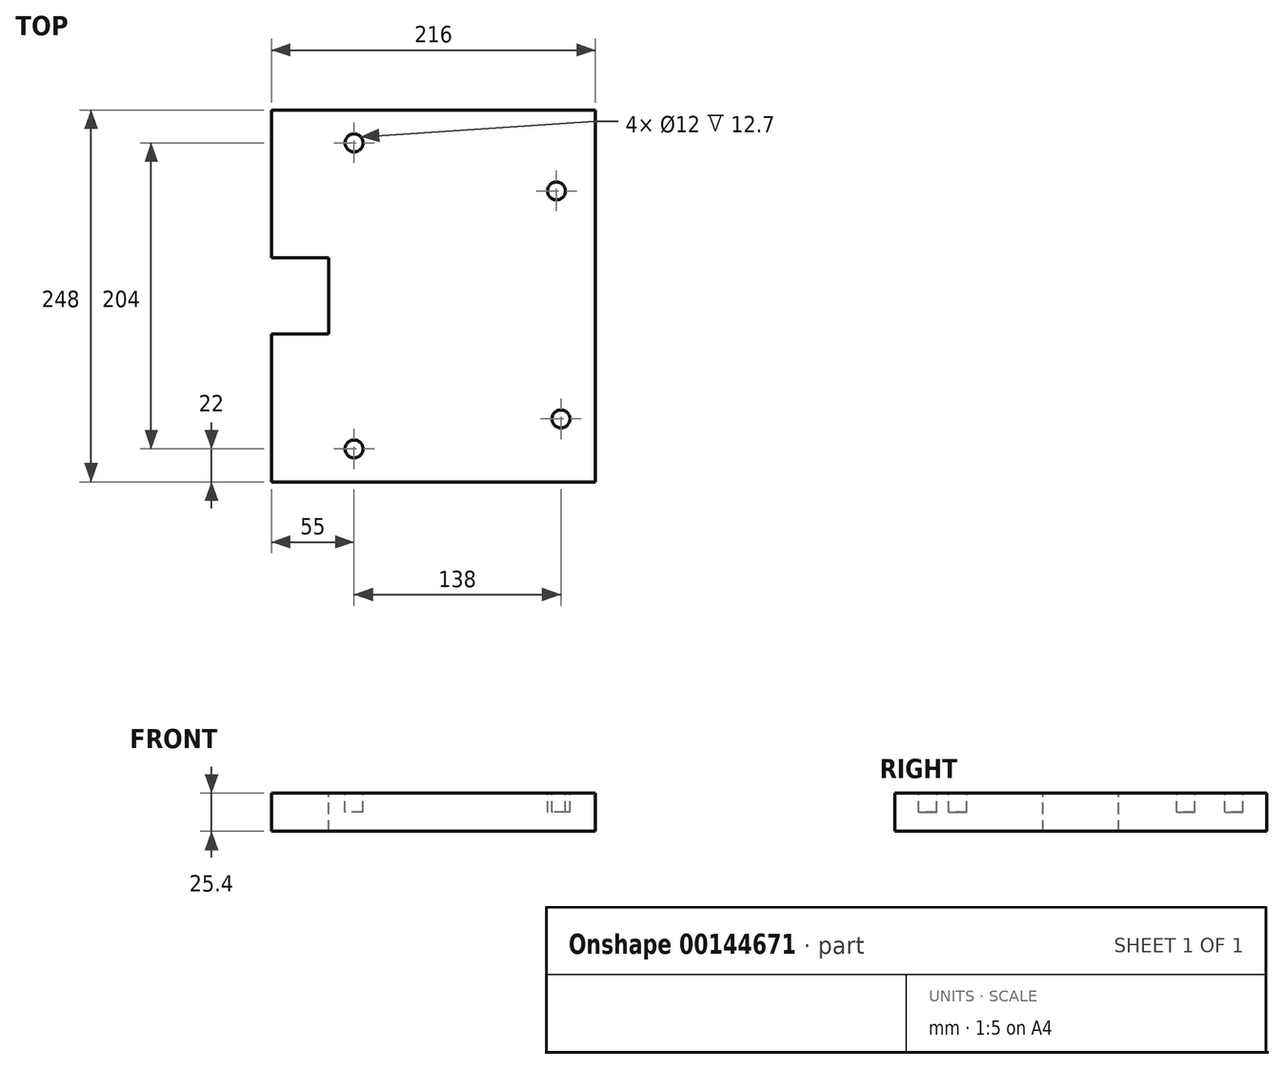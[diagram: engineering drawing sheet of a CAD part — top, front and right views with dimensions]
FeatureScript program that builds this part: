
annotation { "Feature Type Name" : "Feature", "Feature Type Description" : "" }
export const myFeature = defineFeature(function(context is Context, id is Id, definition is map)
    precondition{}
    {
        {
            var Q0;
            Q0=qCreatedBy(makeId("Front.planeOp"),FACE);
            var sketch = newSketch(context, id + "F0", { "sketchPlane" : qUnion([Q0])});
            skLineSegment(sketch, "E0.bottom", {"start": v(0, 0) * mm, "end": v(-216, 0) * mm});
            skLineSegment(sketch, "E0.top", {"start": v(0, 25.4) * mm, "end": v(-216, 25.4) * mm});
            skLineSegment(sketch, "E0.left", {"start": v(0, 0) * mm, "end": v(0, 25.4) * mm});
            skLineSegment(sketch, "E0.right", {"start": v(-216, 0) * mm, "end": v(-216, 25.4) * mm});
            skSolve(sketch);
        }
        {
            var Q0;
            Q0=makeQuery(id+"F0.imprint","IMPRINT",FACE,{"disambiguationData":[TD([[makeQuery(id+"F0.imprint","IMPRINT",EDGE,{"derivedFrom":sQuery(id+"F0.wireOp",EDGE,"E0.bottom")}),-1.0]])]});
            extrude(context, id + "F1", {"entities" : qUnion([Q0]), "oppositeDirection" : true, "depth" : 248 * mm});
        }
        {
            var Q0;
            Q0=makeQuery(id+"F1.opExtrude","SWEPT_FACE",FACE,{"disambiguationData":[OSD([sQuery(id+"F0.wireOp",EDGE,"E0.top")])]});
            var sketch = newSketch(context, id + "F2", { "sketchPlane" : qUnion([Q0])});
            skCircle(sketch, "E1", {"center": v(-26, 194) * mm, "radius": 6 * mm});
            skCircle(sketch, "E2", {"center": v(-23, 42) * mm, "radius": 6 * mm});
            skCircle(sketch, "E3", {"center": v(-161, 226) * mm, "radius": 6 * mm});
            skCircle(sketch, "E4", {"center": v(-161, 22) * mm, "radius": 6 * mm});
            skSolve(sketch);
        }
        {
            var Q0;
            Q0=makeQuery(id+"F2.imprint","IMPRINT",FACE,{"disambiguationData":[TD([[makeQuery(id+"F2.imprint","IMPRINT",EDGE,{"derivedFrom":sQuery(id+"F2.wireOp",EDGE,"E3")}),1.0]])]});
            var Q1;
            Q1=makeQuery(id+"F2.imprint","IMPRINT",FACE,{"disambiguationData":[TD([[makeQuery(id+"F2.imprint","IMPRINT",EDGE,{"derivedFrom":sQuery(id+"F2.wireOp",EDGE,"E4")}),1.0]])]});
            var Q2;
            Q2=makeQuery(id+"F2.imprint","IMPRINT",FACE,{"disambiguationData":[TD([[makeQuery(id+"F2.imprint","IMPRINT",EDGE,{"derivedFrom":sQuery(id+"F2.wireOp",EDGE,"E1")}),1.0]])]});
            var Q3;
            Q3=makeQuery(id+"F2.imprint","IMPRINT",FACE,{"disambiguationData":[TD([[makeQuery(id+"F2.imprint","IMPRINT",EDGE,{"derivedFrom":sQuery(id+"F2.wireOp",EDGE,"E2")}),1.0]])]});
            extrude(context, id + "F3", {"entities" : qUnion([Q0, Q1, Q2, Q3]), "operationType" : NewBodyOperationType.REMOVE, "oppositeDirection" : true, "depth" : 12.7 * mm});
        }
        {
            var Q0;
            Q0=makeQuery(id+"F1.opExtrude","SWEPT_FACE",FACE,{"disambiguationData":[OSD([sQuery(id+"F0.wireOp",EDGE,"E0.top")])]});
            var sketch = newSketch(context, id + "F4", { "sketchPlane" : qUnion([Q0])});
            skLineSegment(sketch, "E5", {"start": v(-216, 248) * mm, "end": v(-216, 149.4) * mm, "construction": true});
            skLineSegment(sketch, "E6", {"start": v(-216, 0) * mm, "end": v(-216, 98.6) * mm, "construction": true});
            skLineSegment(sketch, "E7.bottom", {"start": v(-216, 149.4) * mm, "end": v(-178, 149.4) * mm});
            skLineSegment(sketch, "E7.top", {"start": v(-216, 98.6) * mm, "end": v(-178, 98.6) * mm});
            skLineSegment(sketch, "E7.left", {"start": v(-216, 149.4) * mm, "end": v(-216, 98.6) * mm});
            skLineSegment(sketch, "E7.right", {"start": v(-178, 149.4) * mm, "end": v(-178, 98.6) * mm});
            skSolve(sketch);
        }
        {
            var Q0;
            Q0=makeQuery(id+"F4.imprint","IMPRINT",FACE,{"disambiguationData":[TD([[makeQuery(id+"F4.imprint","IMPRINT",EDGE,{"derivedFrom":sQuery(id+"F4.wireOp",EDGE,"E7.bottom")}),-1.0]])]});
            var Q1;
            Q1=makeQuery(id+"F1.opExtrude","SWEPT_FACE",FACE,{"disambiguationData":[OSD([sQuery(id+"F0.wireOp",EDGE,"E0.bottom")])]});
            extrude(context, id + "F5", {"entities" : qUnion([Q0]), "operationType" : NewBodyOperationType.REMOVE, "endBound" : BoundingType.UP_TO_SURFACE, "oppositeDirection" : true, "endBoundEntityFace" : qUnion([Q1]), "depth" : 25.4 * mm});
        }
    });
